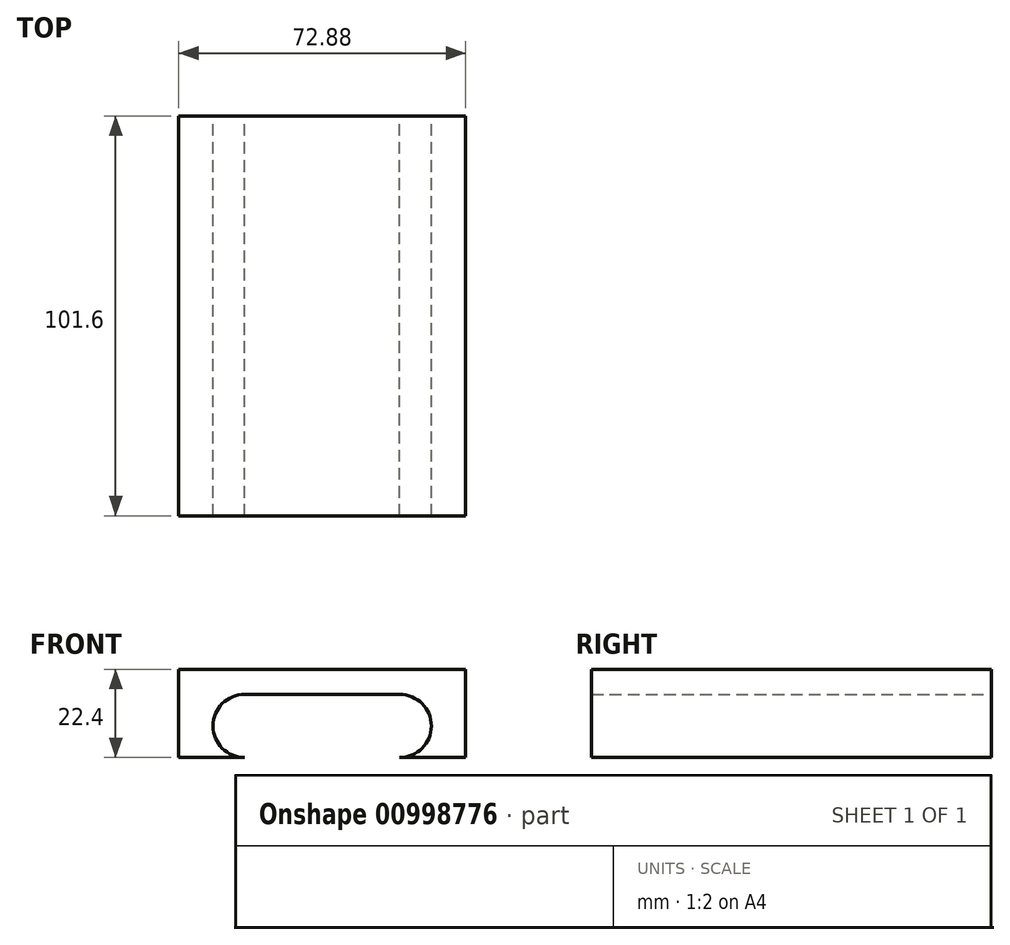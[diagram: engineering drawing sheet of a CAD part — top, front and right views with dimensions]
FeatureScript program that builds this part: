
annotation { "Feature Type Name" : "Feature", "Feature Type Description" : "" }
export const myFeature = defineFeature(function(context is Context, id is Id, definition is map)
    precondition{}
    {
        {
            var Q0;
            Q0=qCreatedBy(makeId("Front.planeOp"),FACE);
            var sketch = newSketch(context, id + "F0", { "sketchPlane" : qUnion([Q0])});
            skLineSegment(sketch, "E0.bottom", {"start": v(-49.69, 34.64) * mm, "end": v(23.19, 34.64) * mm});
            skLineSegment(sketch, "E0.top", {"start": v(-49.69, 28.29) * mm, "end": v(23.19, 28.29) * mm});
            skLineSegment(sketch, "E0.left", {"start": v(-49.69, 34.64) * mm, "end": v(-49.69, 28.29) * mm});
            skLineSegment(sketch, "E0.right", {"start": v(23.19, 34.64) * mm, "end": v(23.19, 28.29) * mm});
            skLineSegment(sketch, "E1.bottom", {"start": v(-49.69, 28.29) * mm, "end": v(-23.7, 28.29) * mm});
            skLineSegment(sketch, "E1.top", {"start": v(-49.69, 12.24) * mm, "end": v(-23.7, 12.24) * mm});
            skLineSegment(sketch, "E1.left", {"start": v(-49.69, 28.29) * mm, "end": v(-49.69, 12.24) * mm});
            skLineSegment(sketch, "E1.right", {"start": v(-23.7, 28.29) * mm, "end": v(-23.7, 12.24) * mm});
            skLineSegment(sketch, "E2.bottom", {"start": v(23.19, 28.29) * mm, "end": v(-2.8, 28.29) * mm});
            skLineSegment(sketch, "E2.top", {"start": v(23.19, 12.24) * mm, "end": v(-2.8, 12.24) * mm});
            skLineSegment(sketch, "E2.left", {"start": v(23.19, 28.29) * mm, "end": v(23.19, 12.24) * mm});
            skLineSegment(sketch, "E2.right", {"start": v(-2.8, 28.29) * mm, "end": v(-2.8, 12.24) * mm});
            skLineSegment(sketch, "E3.bottom", {"start": v(-23.7, 28.29) * mm, "end": v(-2.8, 28.29) * mm});
            skLineSegment(sketch, "E3.top", {"start": v(-23.7, 12.24) * mm, "end": v(-2.8, 12.24) * mm});
            skLineSegment(sketch, "E4", {"start": v(23.19, 20.26) * mm, "end": v(11.53, 20.26) * mm});
            skLineSegment(sketch, "E5", {"start": v(-49.69, 20.26) * mm, "end": v(-38.03, 20.26) * mm});
            skLineSegment(sketch, "E6", {"start": v(-38.03, 20.26) * mm, "end": v(-32.95, 20.26) * mm});
            skLineSegment(sketch, "E7", {"start": v(11.53, 20.26) * mm, "end": v(6.45, 20.26) * mm});
            skCircle(sketch, "E8", {"center": v(-32.95, 20.26) * mm, "radius": 8.03 * mm});
            skCircle(sketch, "E9", {"center": v(6.45, 20.26) * mm, "radius": 8.03 * mm});
            skSolve(sketch);
        }
        {
            var Q0;
            Q0=makeQuery(id+"F0.imprint","IMPRINT",FACE,{"disambiguationData":[TD([[makeQuery(id+"F0.imprint","IMPRINT",EDGE,{"derivedFrom":sQuery(id+"F0.wireOp",EDGE,"E0.bottom")}),-1.0]])]});
            var Q1;
            {var subQ0=sQuery(id+"F0.wireOp",EDGE,"E1.left");var subQ5=sQuery(id+"F0.wireOp",EDGE,"E5");var subQ6=makeQuery(id+"F0.imprint","INTERSECT",VERTEX,{"derivedFrom":[subQ0,subQ5]});Q1=makeQuery(id+"F0.imprint","IMPRINT",FACE,{"disambiguationData":[TD([[makeQuery(id+"F0.imprint","IMPRINT",EDGE,{"disambiguationData":[TD([[subQ6,-1.0]])],"derivedFrom":subQ5}),1.0]])]});}
            var Q2;
            {var subQ0=sQuery(id+"F0.wireOp",EDGE,"E1.left");var subQ1=sQuery(id+"F0.wireOp",EDGE,"E1.top");var subQ2=makeQuery(id+"F0.imprint","INTERSECT",VERTEX,{"derivedFrom":[subQ1,subQ0]});Q2=makeQuery(id+"F0.imprint","IMPRINT",FACE,{"disambiguationData":[TD([[makeQuery(id+"F0.imprint","IMPRINT",EDGE,{"disambiguationData":[TD([[subQ2,-1.0]])],"derivedFrom":subQ1}),1.0]])]});}
            var Q3;
            {var subQ0=sQuery(id+"F0.wireOp",EDGE,"E2.left");var subQ5=sQuery(id+"F0.wireOp",EDGE,"E4");var subQ6=makeQuery(id+"F0.imprint","INTERSECT",VERTEX,{"derivedFrom":[subQ0,subQ5]});Q3=makeQuery(id+"F0.imprint","IMPRINT",FACE,{"disambiguationData":[TD([[makeQuery(id+"F0.imprint","IMPRINT",EDGE,{"disambiguationData":[TD([[subQ6,-1.0]])],"derivedFrom":subQ5}),-1.0]])]});}
            var Q4;
            {var subQ0=sQuery(id+"F0.wireOp",EDGE,"E2.left");var subQ1=sQuery(id+"F0.wireOp",EDGE,"E2.top");var subQ2=makeQuery(id+"F0.imprint","INTERSECT",VERTEX,{"derivedFrom":[subQ1,subQ0]});Q4=makeQuery(id+"F0.imprint","IMPRINT",FACE,{"disambiguationData":[TD([[makeQuery(id+"F0.imprint","IMPRINT",EDGE,{"disambiguationData":[TD([[subQ2,-1.0]])],"derivedFrom":subQ1}),-1.0]])]});}
            extrude(context, id + "F1", {"entities" : qUnion([Q0, Q1, Q2, Q3, Q4]), "depth" : 101.6 * mm, "offsetDistance" : 25.4 * mm});
        }
    });
